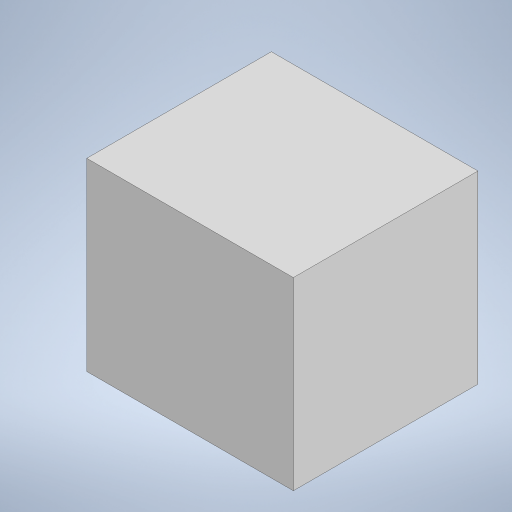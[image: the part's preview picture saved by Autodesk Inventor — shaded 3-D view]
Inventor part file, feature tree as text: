
AUTODESK INVENTOR PART (.ipt)
format: ipt  version: 2024 (Build 280153000, 153)  size: 182,272 bytes
history: native  units: in
note: dims shown in document units (in); Inventor stores cm internally (conversion verified against a paired STEP export)
features: extrude x3, sketch x3
ambient origin geometry x8: Origin, YZ Plane, XZ Plane, XY Plane, X Axis, Y Axis, Z Axis, Center Point
bodies: Solid1 (feature_tree)
feature tree (6):
  extrude  "Extrusion1"  Depth=1.6535in
  extrude  "Extrusion2"  Depth=1.8504in
  extrude  "Extrusion3"  Depth=0.4724in
  sketch  "Sketch1"  dims[d0=1.6535in d1=1.6535in]
  sketch  "Sketch2"  dims[d2=1.8504in d3=0.0in d4=0.1969in]
  sketch  "Sketch3"  dims[d5=0.4724in d6=0.0in d7=0.6102in d8=0.6102in d9=0.1575in d10=0.4724in d11=0.0in]
